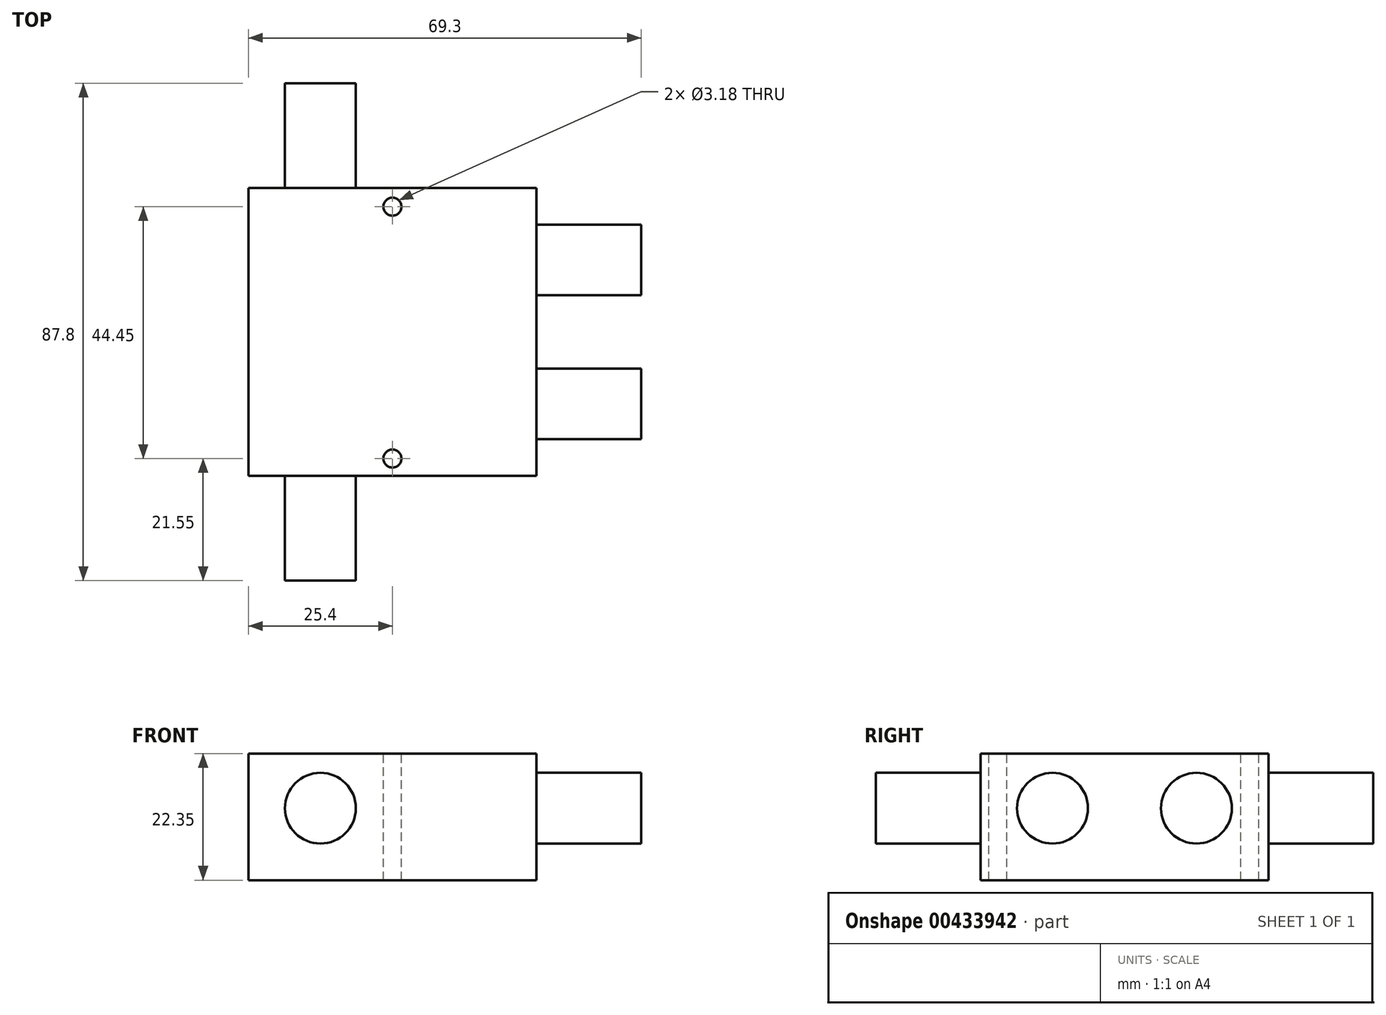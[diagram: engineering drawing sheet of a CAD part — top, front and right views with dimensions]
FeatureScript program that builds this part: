
annotation { "Feature Type Name" : "Feature", "Feature Type Description" : "" }
export const myFeature = defineFeature(function(context is Context, id is Id, definition is map)
    precondition{}
    {
        {
            var Q0;
            Q0=qCreatedBy(makeId("Top.planeOp"),FACE);
            var sketch = newSketch(context, id + "F0", { "sketchPlane" : qUnion([Q0])});
            skLineSegment(sketch, "E0.bottom", {"start": v(-25.4, 25.4) * mm, "end": v(25.4, 25.4) * mm});
            skLineSegment(sketch, "E0.top", {"start": v(-25.4, -25.4) * mm, "end": v(25.4, -25.4) * mm});
            skLineSegment(sketch, "E0.left", {"start": v(-25.4, 25.4) * mm, "end": v(-25.4, -25.4) * mm});
            skLineSegment(sketch, "E0.right", {"start": v(25.4, 25.4) * mm, "end": v(25.4, -25.4) * mm});
            skSolve(sketch);
        }
        {
            var Q0;
            Q0 = qSketchRegion(id + "F0", true);
            extrude(context, id + "F1", {"entities" : qUnion([Q0]), "depth" : 22.35 * mm});
        }
        {
            assignVariable(context, id + "F2", {"name" : "B", "anyValue" : 18.5});
        }
        {
            var Q0;
            Q0=makeQuery(id+"F1.opExtrude","SWEPT_FACE",FACE,{"disambiguationData":[OSD([sQuery(id+"F0.wireOp",EDGE,"E0.right")])]});
            var sketch = newSketch(context, id + "F3", { "sketchPlane" : qUnion([Q0])});
            skCircle(sketch, "E1", {"center": v(-12.7, 12.7) * mm, "radius": 6.25 * mm});
            skCircle(sketch, "E2", {"center": v(12.7, 12.7) * mm, "radius": 6.25 * mm});
            skSolve(sketch);
        }
        {
            var Q0;
            Q0 = qSketchRegion(id + "F3", true);
            extrude(context, id + "F4", {"entities" : qUnion([Q0]), "depth" : (getVariable(context, 'B')) * mm});
        }
        {
            var Q0;
            Q0=makeQuery(id+"F1.opExtrude","SWEPT_FACE",FACE,{"disambiguationData":[OSD([sQuery(id+"F0.wireOp",EDGE,"E0.top")])]});
            var sketch = newSketch(context, id + "F5", { "sketchPlane" : qUnion([Q0])});
            skCircle(sketch, "E3", {"center": v(-12.7, 12.7) * mm, "radius": 6.25 * mm});
            skSolve(sketch);
        }
        {
            var Q0;
            Q0 = qSketchRegion(id + "F5", true);
            extrude(context, id + "F6", {"entities" : qUnion([Q0]), "depth" : (getVariable(context, 'B')) * mm});
        }
        {
            var Q0;
            Q0=makeQuery(id+"F1.opExtrude","SWEPT_FACE",FACE,{"disambiguationData":[OSD([sQuery(id+"F0.wireOp",EDGE,"E0.bottom")])]});
            var sketch = newSketch(context, id + "F7", { "sketchPlane" : qUnion([Q0])});
            skCircle(sketch, "E4", {"center": v(12.7, 12.7) * mm, "radius": 6.25 * mm});
            skSolve(sketch);
        }
        {
            var Q0;
            Q0 = qSketchRegion(id + "F7", true);
            extrude(context, id + "F8", {"entities" : qUnion([Q0]), "depth" : (getVariable(context, 'B')) * mm});
        }
        {
            var Q0;
            Q0=makeQuery(id+"F1.opExtrude","CAP_FACE",FACE,{"disambiguationData":[OSD([sQuery(id+"F0.wireOp",EDGE,"E0.bottom"),sQuery(id+"F0.wireOp",EDGE,"E0.top"),sQuery(id+"F0.wireOp",EDGE,"E0.left"),sQuery(id+"F0.wireOp",EDGE,"E0.right")])],"isStart":false});
            var sketch = newSketch(context, id + "F9", { "sketchPlane" : qUnion([Q0])});
            skCircle(sketch, "E5", {"center": v(0, 22.1) * mm, "radius": 1.59 * mm});
            skCircle(sketch, "E6", {"center": v(0, -22.35) * mm, "radius": 1.59 * mm});
            skSolve(sketch);
        }
        {
            var Q0;
            Q0 = qSketchRegion(id + "F9", true);
            extrude(context, id + "F10", {"entities" : qUnion([Q0]), "operationType" : NewBodyOperationType.REMOVE, "endBound" : BoundingType.THROUGH_ALL, "oppositeDirection" : true, "depth" : 25 * mm});
        }
    });
